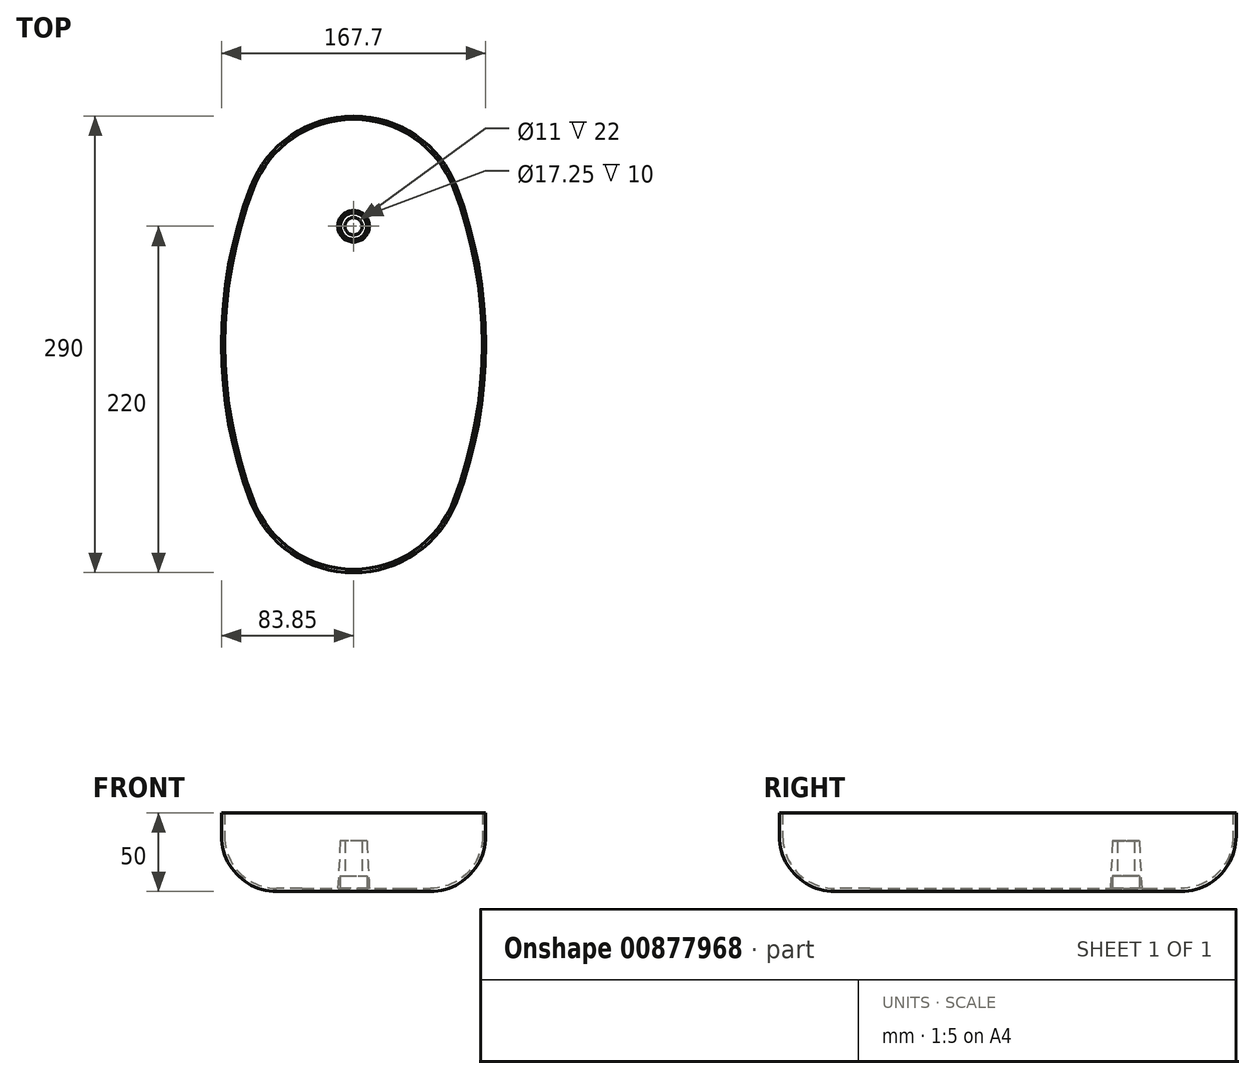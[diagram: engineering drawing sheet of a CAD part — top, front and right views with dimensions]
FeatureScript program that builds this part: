
annotation { "Feature Type Name" : "Feature", "Feature Type Description" : "" }
export const myFeature = defineFeature(function(context is Context, id is Id, definition is map)
    precondition{}
    {
        {
            var Q0;
            Q0=qCreatedBy(makeId("Top.planeOp"),FACE);
            var sketch = newSketch(context, id + "F0", { "sketchPlane" : qUnion([Q0])});
            skArc(sketch, "E0", {"start": v(-65.38, 100) * mm, "mid": v(-83.85, 0) * mm, "end": v(-65.38, -100) * mm});
            skArc(sketch, "E1.MirrorCS", {"start": v(65.38, 100) * mm, "mid": v(83.85, 0) * mm, "end": v(65.38, -100) * mm});
            skArc(sketch, "E2", {"start": v(65.38, 100) * mm, "mid": v(0, 145) * mm, "end": v(-65.38, 100) * mm});
            skArc(sketch, "E3", {"start": v(-65.38, -100) * mm, "mid": v(0, -145) * mm, "end": v(65.38, -100) * mm});
            skSolve(sketch);
        }
        {
            var Q0;
            Q0 = qSketchRegion(id + "F0", true);
            extrude(context, id + "F1", {"entities" : qUnion([Q0]), "depth" : 50 * mm, "offsetDistance" : 25 * mm});
        }
        {
            var Q0;
            Q0=makeQuery(id+"F1.opExtrude","CAP_EDGE",EDGE,{"disambiguationData":[OSD([sQuery(id+"F0.wireOp",EDGE,"E3")])],"isStart":true});
            fillet(context, id + "F2", {"entities" : qUnion([Q0]), "radius" : 35 * mm, "tangentPropagation" : true, "allowEdgeOverflow" : false});
        }
        {
            var Q0;
            Q0=makeQuery(id+"F1.opExtrude","CAP_FACE",FACE,{"disambiguationData":[OSD([sQuery(id+"F0.wireOp",EDGE,"E0"),sQuery(id+"F0.wireOp",EDGE,"E1.MirrorCS"),sQuery(id+"F0.wireOp",EDGE,"E2"),sQuery(id+"F0.wireOp",EDGE,"E3")])],"isStart":false});
            shell(context, id + "F3", {"entities" : qUnion([Q0]), "thickness" : 2 * mm});
        }
        {
            var Q0;
            Q0=makeQuery(id+"F3.opShell","OFFSET_FACE",FACE,{"disambiguationData":[OSD([sQuery(id+"F0.wireOp",EDGE,"E0"),sQuery(id+"F0.wireOp",EDGE,"E1.MirrorCS"),sQuery(id+"F0.wireOp",EDGE,"E2"),sQuery(id+"F0.wireOp",EDGE,"E3")])]});
            var sketch = newSketch(context, id + "F4", { "sketchPlane" : qUnion([Q0])});
            skCircle(sketch, "E4", {"center": v(0, 75) * mm, "radius": 10 * mm});
            skSolve(sketch);
        }
        {
            var Q0;
            Q0 = qSketchRegion(id + "F4", true);
            extrude(context, id + "F5", {"entities" : qUnion([Q0]), "operationType" : NewBodyOperationType.ADD, "depth" : 30 * mm, "offsetDistance" : 25 * mm, "hasDraft" : true, "draftAngle" : 3 * degree, "draftPullDirection" : true});
        }
        {
            var Q0;
            Q0=makeQuery(id+"F1.opExtrude","CAP_FACE",FACE,{"disambiguationData":[OSD([sQuery(id+"F0.wireOp",EDGE,"E0"),sQuery(id+"F0.wireOp",EDGE,"E1.MirrorCS"),sQuery(id+"F0.wireOp",EDGE,"E2"),sQuery(id+"F0.wireOp",EDGE,"E3")])],"isStart":true});
            var sketch = newSketch(context, id + "F6", { "sketchPlane" : qUnion([Q0])});
            skPoint(sketch, "E5", {"position": v(0, -75) * mm});
            skSolve(sketch);
        }
        {
            var Q0;
            Q0=sQuery(id+"F6.wireOp",VERTEX,"E5");
            var Q1;
            Q1=makeQuery(id+"F1.opExtrude","SWEPT_BODY",BODY,{"disambiguationData":[OSD([sQuery(id+"F0.wireOp",EDGE,"E0"),sQuery(id+"F0.wireOp",EDGE,"E1.MirrorCS"),sQuery(id+"F0.wireOp",EDGE,"E2"),sQuery(id+"F0.wireOp",EDGE,"E3")])]});
            hole(context, id + "F7", {"style" : HoleStyle.C_BORE, "endStyle" : HoleEndStyle.THROUGH, "standardTappedOrClearance" : lookupTablePath({ "fit" : "Normal", "standard" : "ISO", "size" : "M10", "type" : "Clearance" }), "standardBlindInLast" : lookupTablePath({ "fit" : "Normal", "standard" : "ISO", "size" : "M10", "type" : "Clearance" }), "holeDiameter" : 11 * mm, "cBoreDiameter" : 17.25 * mm, "cBoreDepth" : 10 * mm, "majorDiameter" : 5 * mm, "isTappedThrough" : true, "tappedDepth" : 12 * mm, "tapClearance" : 3, "locations" : qUnion([Q0]), "scope" : qUnion([Q1])});
        }
        {
            var Q0;
            Q0=qCreatedBy(makeId("Front.planeOp"),FACE);
            cPlane(context, id + "F8", {"entities" : qUnion([Q0]), "cplaneType" : CPlaneType.OFFSET, "offset" : 40 * mm, "width" : 150 * mm, "height" : 150 * mm});
        }
    });
